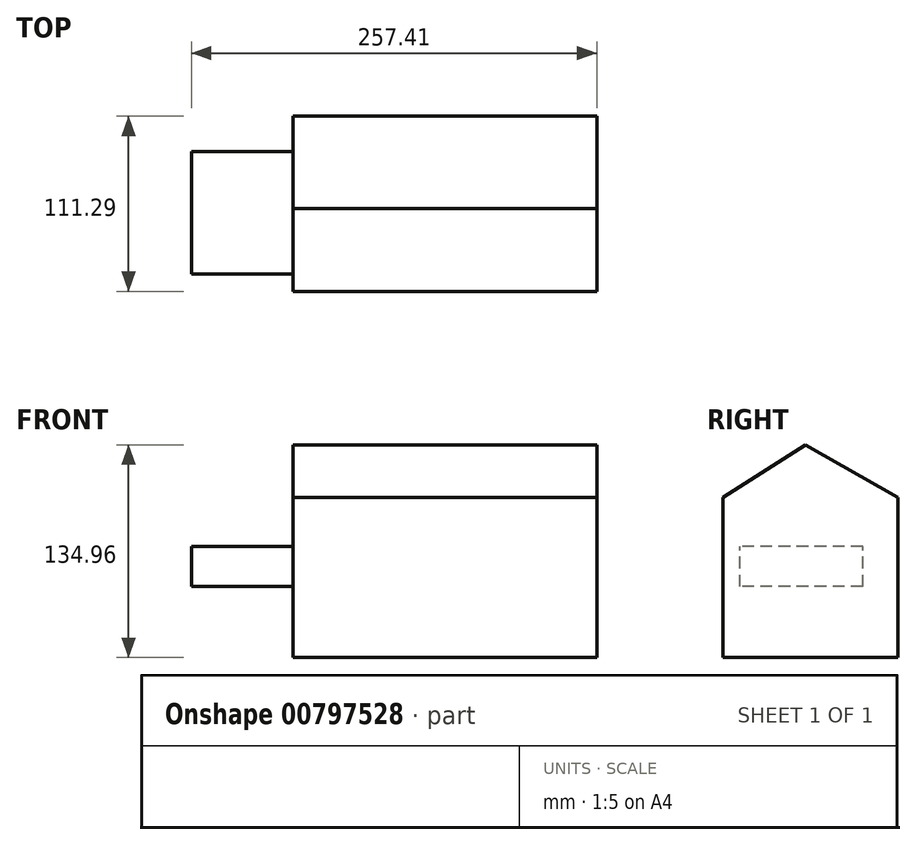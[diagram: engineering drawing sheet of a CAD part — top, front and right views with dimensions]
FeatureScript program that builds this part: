
annotation { "Feature Type Name" : "Feature", "Feature Type Description" : "" }
export const myFeature = defineFeature(function(context is Context, id is Id, definition is map)
    precondition{}
    {
        {
            var Q0;
            Q0=qCreatedBy(makeId("Right.planeOp"),FACE);
            var sketch = newSketch(context, id + "F0", { "sketchPlane" : qUnion([Q0])});
            skLineSegment(sketch, "E0.bottom", {"start": v(-52.52, -44.94) * mm, "end": v(58.77, -44.94) * mm});
            skLineSegment(sketch, "E0.left", {"start": v(-52.52, -44.94) * mm, "end": v(-52.52, 56.47) * mm});
            skLineSegment(sketch, "E0.right", {"start": v(58.77, -44.94) * mm, "end": v(58.77, 56.47) * mm});
            skLineSegment(sketch, "E1", {"start": v(-52.52, 56.47) * mm, "end": v(0, 90.02) * mm});
            skLineSegment(sketch, "E2", {"start": v(0, 90.02) * mm, "end": v(58.77, 56.47) * mm});
            skSolve(sketch);
        }
        {
            var Q0;
            Q0=makeQuery(id+"F0.imprint","IMPRINT",FACE,{"disambiguationData":[TD([[makeQuery(id+"F0.imprint","IMPRINT",EDGE,{"derivedFrom":sQuery(id+"F0.wireOp",EDGE,"E0.bottom")}),1.0]])]});
            extrude(context, id + "F1", {"entities" : qUnion([Q0]), "depth" : 193.04 * mm, "offsetDistance" : 25.4 * mm});
        }
        {
            var Q0;
            Q0=qCreatedBy(makeId("Top.planeOp"),FACE);
            var sketch = newSketch(context, id + "F2", { "sketchPlane" : qUnion([Q0])});
            skLineSegment(sketch, "E3.bottom", {"start": v(-64.37, 36.38) * mm, "end": v(58.44, 36.38) * mm});
            skLineSegment(sketch, "E3.top", {"start": v(-64.37, -41.65) * mm, "end": v(58.44, -41.65) * mm});
            skLineSegment(sketch, "E3.left", {"start": v(-64.37, 36.38) * mm, "end": v(-64.37, -41.65) * mm});
            skLineSegment(sketch, "E3.right", {"start": v(58.44, 36.38) * mm, "end": v(58.44, -41.65) * mm});
            skSolve(sketch);
        }
        {
            var Q0;
            Q0 = qSketchRegion(id + "F2", true);
            var Q1;
            Q1 = qSketchRegion(id + "F5xA5dD1j05HQb6_1", true);
            extrude(context, id + "F3", {"entities" : qUnion([Q0, Q1]), "operationType" : NewBodyOperationType.ADD, "depth" : 25.4 * mm, "offsetDistance" : 25.4 * mm});
        }
    });
